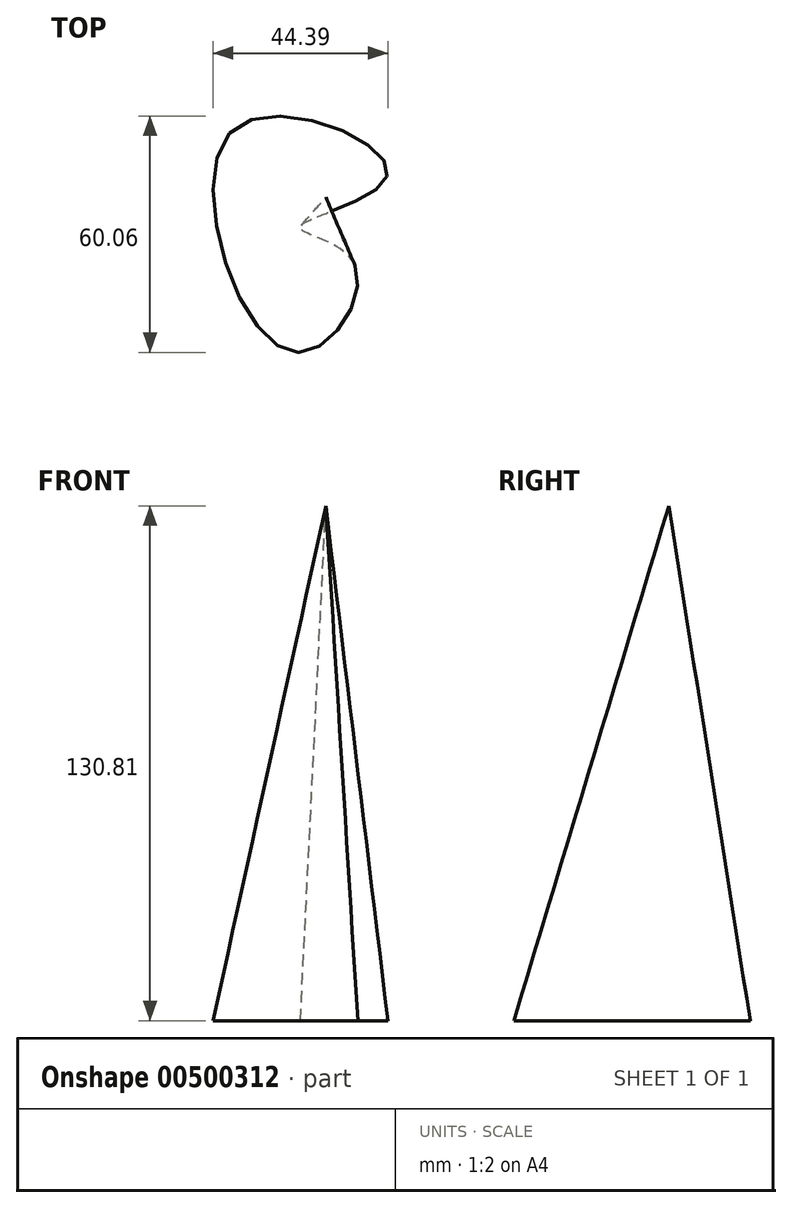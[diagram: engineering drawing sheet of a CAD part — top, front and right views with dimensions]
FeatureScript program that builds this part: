
annotation { "Feature Type Name" : "Feature", "Feature Type Description" : "" }
export const myFeature = defineFeature(function(context is Context, id is Id, definition is map)
    precondition{}
    {
        {
            var Q0;
            Q0=qCreatedBy(makeId("Top.planeOp"),FACE);
            var sketch = newSketch(context, id + "F0", { "sketchPlane" : qUnion([Q0])});
            skFitSpline(sketch, "E0", {"points": [v(-23.32, 17.34) * mm, v(-8.74, -39.2) * mm, v(7.29, -17.05) * mm, v(-6.41, -7.43) * mm, v(15.74, 5.98) * mm, v(-23.32, 17.34) * mm]});
            skSolve(sketch);
        }
        {
            var Q0;
            Q0=qCreatedBy(makeId("Top.planeOp"),FACE);
            cPlane(context, id + "F1", {"entities" : qUnion([Q0]), "cplaneType" : CPlaneType.OFFSET, "offset" : 130.8 * mm, "width" : 152.4 * mm, "height" : 152.4 * mm});
        }
        {
            var Q0;
            Q0=qCreatedBy(id+"F1.planeOp",FACE);
            var sketch = newSketch(context, id + "F2", { "sketchPlane" : qUnion([Q0])});
            skPoint(sketch, "E1", {"position": v(0, 0) * mm});
            skSolve(sketch);
        }
        {
            var Q0;
            Q0=sQuery(id+"F2.wireOp",VERTEX,"E1");
            var Q1;
            Q1=makeQuery(id+"F0.imprint","IMPRINT",FACE,{"disambiguationData":[TD([[makeQuery(id+"F0.imprint","IMPRINT",EDGE,{"derivedFrom":sQuery(id+"F0.wireOp",EDGE,"E0")}),1.0]])]});
            loft(context, id + "F3", {"sheetProfilesArray" : [{ "sheetProfileEntities" : qUnion([Q0]) }, { "sheetProfileEntities" : qUnion([Q1]) }]});
        }
    });
